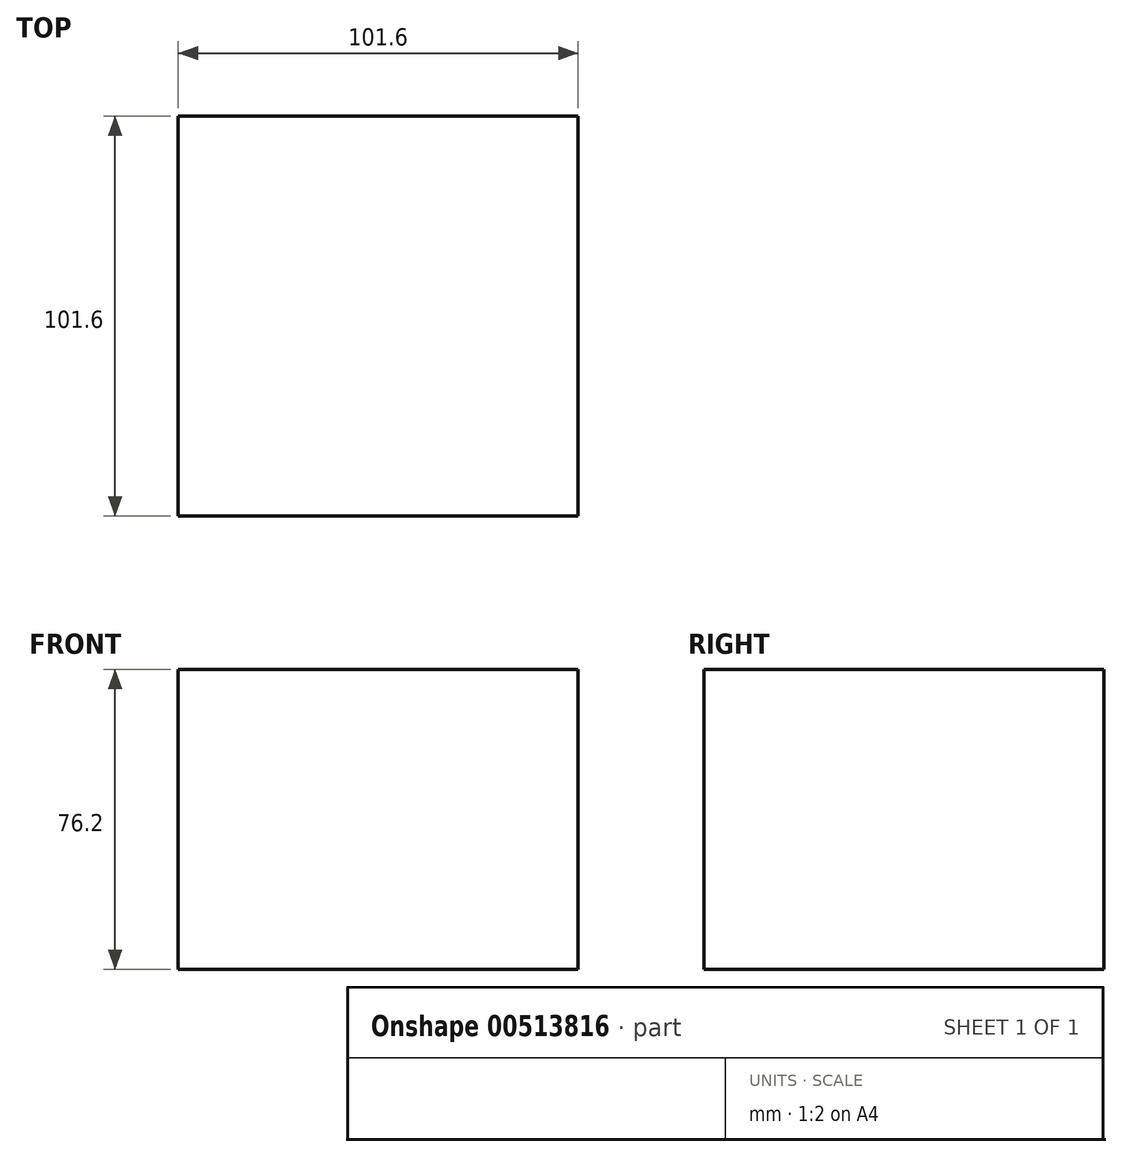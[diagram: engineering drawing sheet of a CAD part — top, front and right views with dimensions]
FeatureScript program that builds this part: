
annotation { "Feature Type Name" : "Feature", "Feature Type Description" : "" }
export const myFeature = defineFeature(function(context is Context, id is Id, definition is map)
    precondition{}
    {
        {
            var Q0;
            Q0=qCreatedBy(makeId("Top.planeOp"),FACE);
            var sketch = newSketch(context, id + "F0", { "sketchPlane" : qUnion([Q0])});
            skLineSegment(sketch, "E0.bottom", {"start": v(50.8, 55) * mm, "end": v(-50.8, 55) * mm});
            skLineSegment(sketch, "E0.top", {"start": v(50.8, -46.6) * mm, "end": v(-50.8, -46.6) * mm});
            skLineSegment(sketch, "E0.left", {"start": v(50.8, 55) * mm, "end": v(50.8, -46.6) * mm});
            skLineSegment(sketch, "E0.right", {"start": v(-50.8, 55) * mm, "end": v(-50.8, -46.6) * mm});
            skPoint(sketch, "E0.middle", {"position": v(0, 4.2) * mm});
            skCircle(sketch, "E1", {"center": v(0, 4.2) * mm, "radius": 38.1 * mm});
            skSolve(sketch);
        }
        {
            var Q0;
            Q0 = qSketchRegion(id + "F0", true);
            var Q1;
            Q1=makeQuery(id+"F0.imprint","IMPRINT",FACE,{"disambiguationData":[TD([[makeQuery(id+"F0.imprint","IMPRINT",EDGE,{"derivedFrom":sQuery(id+"F0.wireOp",EDGE,"E1")}),1.0]])]});
            extrude(context, id + "F1", {"entities" : qUnion([Q0, Q1]), "depth" : 76.2 * mm});
        }
    });
